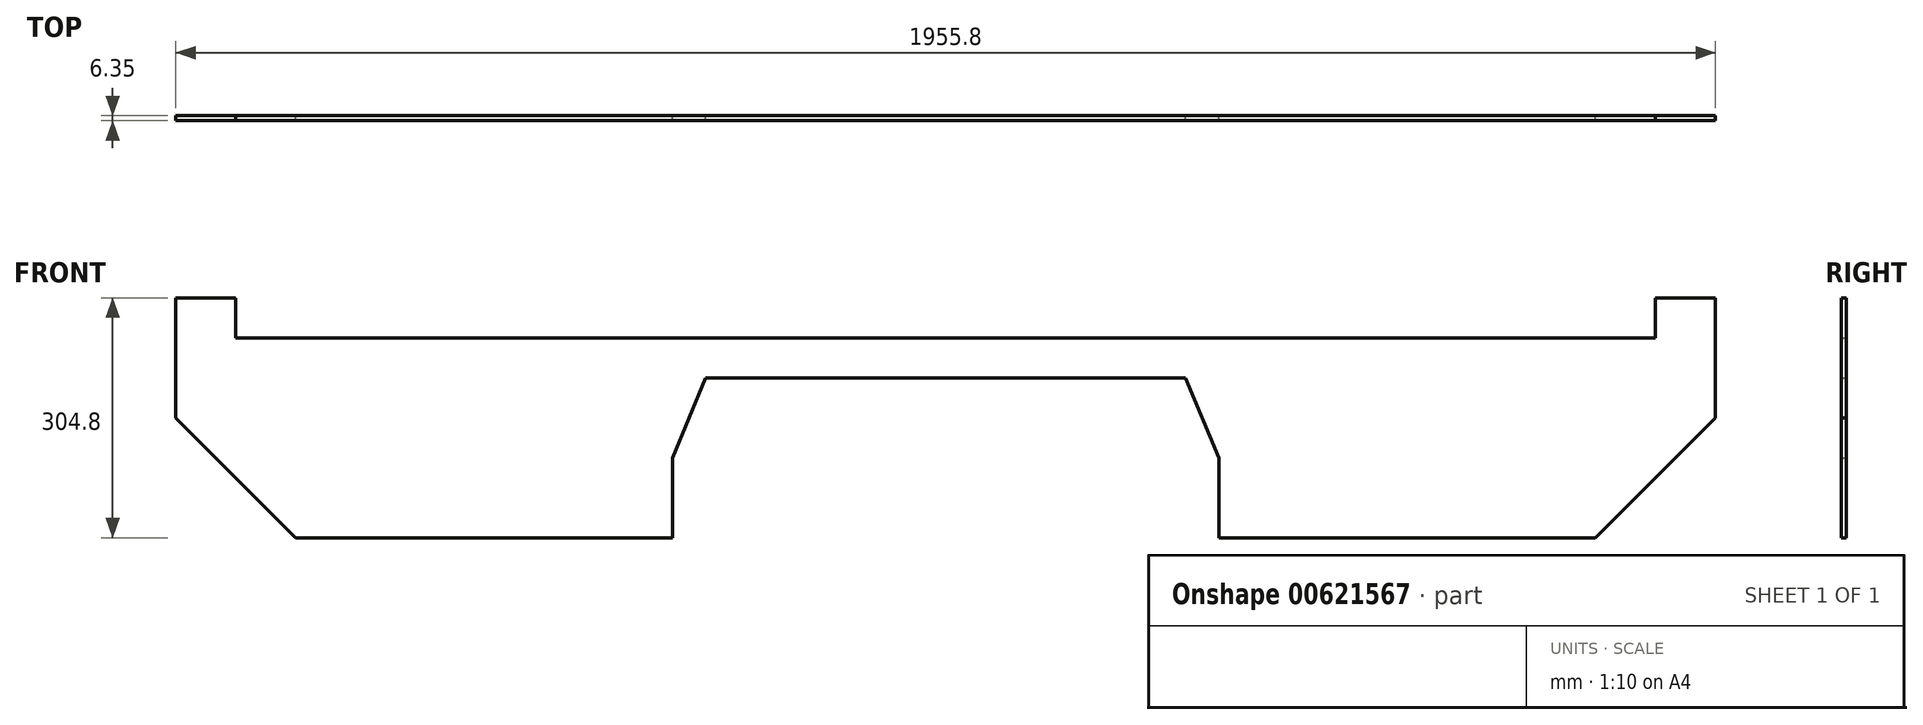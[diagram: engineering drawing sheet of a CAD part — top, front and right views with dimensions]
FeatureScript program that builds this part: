
annotation { "Feature Type Name" : "Feature", "Feature Type Description" : "" }
export const myFeature = defineFeature(function(context is Context, id is Id, definition is map)
    precondition{}
    {
        {
            var Q0;
            Q0=qCreatedBy(makeId("Front.planeOp"),FACE);
            var sketch = newSketch(context, id + "F0", { "sketchPlane" : qUnion([Q0])});
            skLineSegment(sketch, "E0.bottom", {"start": v(977.9, 152.4) * mm, "end": v(901.7, 152.4) * mm});
            skLineSegment(sketch, "E0.top", {"start": v(825.5, -152.4) * mm, "end": v(346.88, -152.4) * mm});
            skPoint(sketch, "E0.middle", {"position": v(0, 0) * mm});
            skLineSegment(sketch, "E1.0", {"start": v(901.7, 101.6) * mm, "end": v(-901.7, 101.6) * mm});
            skLineSegment(sketch, "E2.0", {"start": v(901.7, 152.4) * mm, "end": v(901.7, 101.6) * mm});
            skLineSegment(sketch, "E3.0", {"start": v(-901.7, 152.4) * mm, "end": v(-901.7, 101.6) * mm});
            skLineSegment(sketch, "E4.trimOffspring", {"start": v(-901.7, 152.4) * mm, "end": v(-977.9, 152.4) * mm});
            skLineSegment(sketch, "E5", {"start": v(977.9, 0) * mm, "end": v(825.5, -152.4) * mm});
            skLineSegment(sketch, "E6", {"start": v(977.9, 0) * mm, "end": v(977.9, 152.4) * mm});
            skPoint(sketch, "E7.start.orphan", {"position": v(977.9, -152.4) * mm});
            skLineSegment(sketch, "E8", {"start": v(-977.9, 152.4) * mm, "end": v(-977.9, 0) * mm});
            skLineSegment(sketch, "E9", {"start": v(-977.9, 0) * mm, "end": v(-825.5, -152.4) * mm});
            skPoint(sketch, "E10.orphan", {"position": v(-977.9, -152.4) * mm});
            skLineSegment(sketch, "E11", {"start": v(0, 101.6) * mm, "end": v(0, 50.8) * mm});
            skPoint(sketch, "E11.endSnap0", {"position": v(0, 101.6) * mm});
            skLineSegment(sketch, "E12.MirrorCS", {"start": v(0, 50.8) * mm, "end": v(-304.8, 50.8) * mm});
            skLineSegment(sketch, "E13", {"start": v(-304.8, 50.8) * mm, "end": v(-346.88, -50.8) * mm});
            skLineSegment(sketch, "E14", {"start": v(-346.88, -50.8) * mm, "end": v(-346.88, -152.4) * mm});
            skLineSegment(sketch, "E15.MirrorCS", {"start": v(0, 50.8) * mm, "end": v(304.8, 50.8) * mm});
            skLineSegment(sketch, "E16.MirrorCS", {"start": v(304.8, 50.8) * mm, "end": v(346.88, -50.8) * mm});
            skLineSegment(sketch, "E17.MirrorCS", {"start": v(346.88, -50.8) * mm, "end": v(346.88, -152.4) * mm});
            skLineSegment(sketch, "E18.trimOffspring", {"start": v(-346.88, -152.4) * mm, "end": v(-825.5, -152.4) * mm});
            skSolve(sketch);
        }
        {
            var Q0;
            {var subQ0=sQuery(id+"F0.wireOp",EDGE,"E3.0");Q0=makeQuery(id+"F0.imprint","IMPRINT",FACE,{"disambiguationData":[TD([[makeQuery(id+"F0.imprint","IMPRINT",EDGE,{"derivedFrom":subQ0}),-1.0]])]});}
            var Q1;
            Q1=makeQuery(id+"F0.imprint","IMPRINT",FACE,{"disambiguationData":[TD([[makeQuery(id+"F0.imprint","IMPRINT",EDGE,{"derivedFrom":sQuery(id+"F0.wireOp",EDGE,"E0.bottom")}),1.0]])]});
            extrude(context, id + "F1", {"entities" : qUnion([Q0, Q1]), "depth" : 6.35 * mm, "offsetDistance" : 25.4 * mm});
        }
    });
